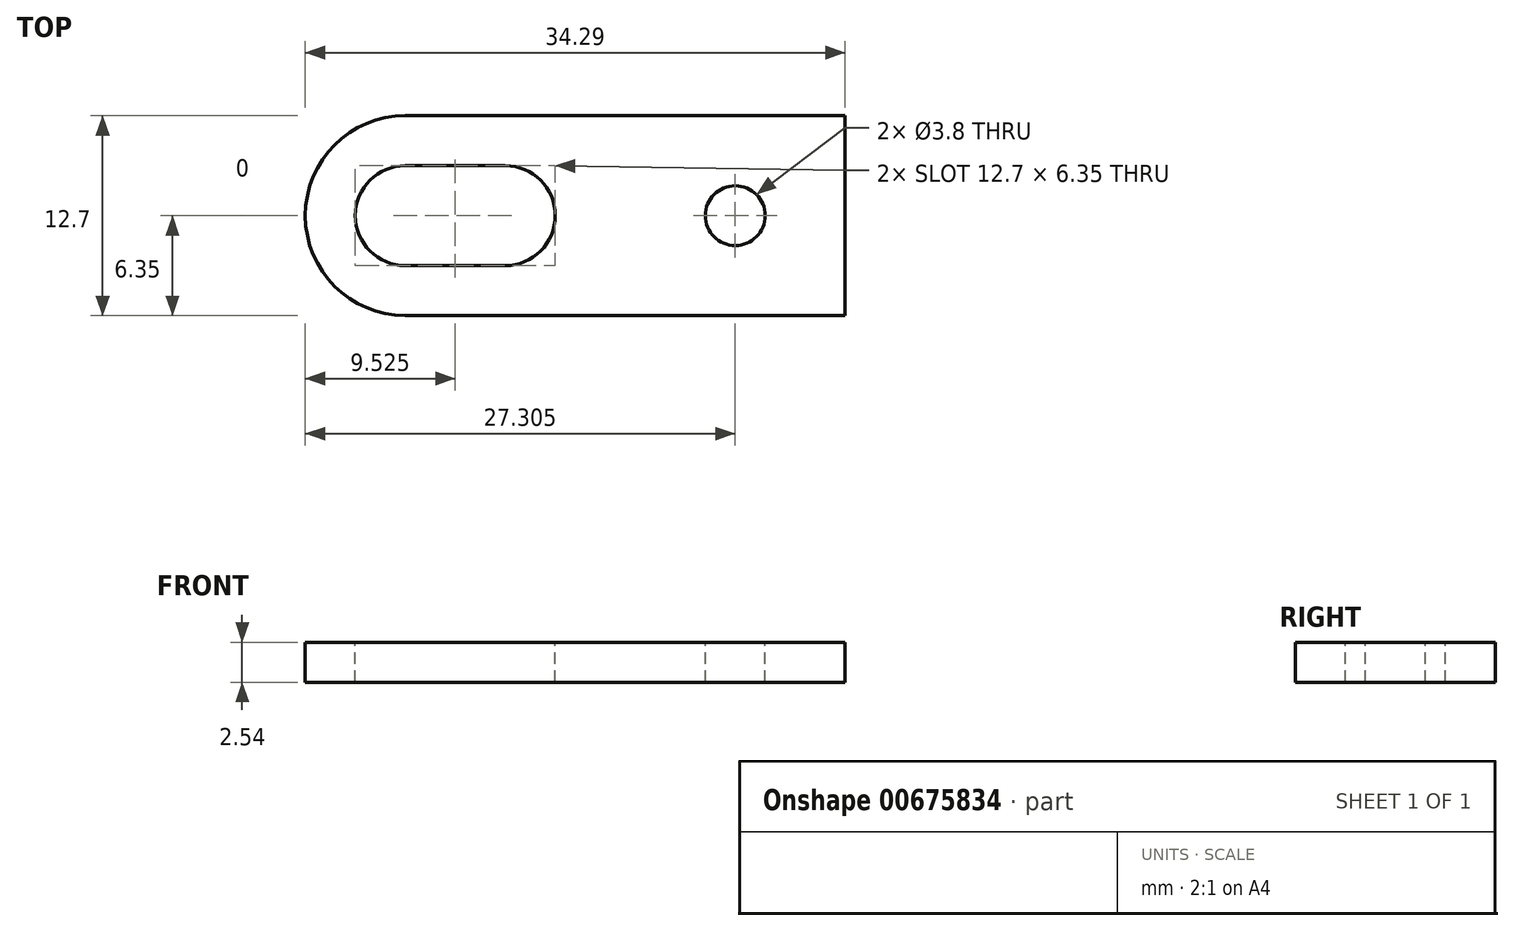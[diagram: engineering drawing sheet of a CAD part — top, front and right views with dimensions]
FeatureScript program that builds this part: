
annotation { "Feature Type Name" : "Feature", "Feature Type Description" : "" }
export const myFeature = defineFeature(function(context is Context, id is Id, definition is map)
    precondition{}
    {
        {
            var Q0;
            Q0=qCreatedBy(makeId("Top.planeOp"),FACE);
            var sketch = newSketch(context, id + "F0", { "sketchPlane" : qUnion([Q0])});
            skLineSegment(sketch, "E0.bottom", {"start": v(6.35, 0) * mm, "end": v(34.3, 0) * mm});
            skLineSegment(sketch, "E0.top", {"start": v(6.35, 12.7) * mm, "end": v(34.3, 12.7) * mm});
            skLineSegment(sketch, "E0.left", {"start": v(0, 6.35) * mm, "end": v(0, 6.35) * mm});
            skLineSegment(sketch, "E0.right", {"start": v(34.3, 0) * mm, "end": v(34.3, 12.7) * mm});
            skPoint(sketch, "E1.visualSharp", {"position": v(0, 12.7) * mm});
            skArc(sketch, "E1.filletArc", {"start": v(6.35, 12.7) * mm, "mid": v(1.86, 10.84) * mm, "end": v(0, 6.35) * mm});
            skPoint(sketch, "E2.visualSharp", {"position": v(0, 0) * mm});
            skArc(sketch, "E2.filletArc", {"start": v(0, 6.35) * mm, "mid": v(1.86, 1.86) * mm, "end": v(6.35, 0) * mm});
            skPoint(sketch, "E3.visualSharp", {"position": v(34.3, 12.7) * mm});
            skSolve(sketch);
        }
        {
            var Q0;
            Q0=qSketchRegion(id+"F0",true);
            extrude(context, id + "F1", {"entities" : qUnion([Q0]), "depth" : 2.54 * mm, "offsetDistance" : 25.4 * mm});
        }
        {
            var Q0;
            Q0=makeQuery(id+"F1.opExtrude","CAP_FACE",FACE,{"disambiguationData":[OSD([sQuery(id+"F0.wireOp",EDGE,"E0.bottom"),sQuery(id+"F0.wireOp",EDGE,"E0.top"),sQuery(id+"F0.wireOp",EDGE,"E0.left"),sQuery(id+"F0.wireOp",EDGE,"E0.right")])],"isStart":false});
            var sketch = newSketch(context, id + "F2", { "sketchPlane" : qUnion([Q0])});
            skArc(sketch, "E4", {"start": v(6.35, 9.53) * mm, "mid": v(3.17, 6.35) * mm, "end": v(6.35, 3.18) * mm});
            skLineSegment(sketch, "E5", {"start": v(0, 6.35) * mm, "end": v(34.3, 6.35) * mm, "construction": true});
            skArc(sketch, "E6", {"start": v(12.7, 3.18) * mm, "mid": v(15.87, 6.35) * mm, "end": v(12.7, 9.53) * mm});
            skLineSegment(sketch, "E7", {"start": v(6.35, 9.53) * mm, "end": v(12.7, 9.53) * mm});
            skLineSegment(sketch, "E8", {"start": v(12.7, 3.18) * mm, "end": v(6.35, 3.18) * mm});
            skSolve(sketch);
        }
        {
            var Q0;
            Q0=qSketchRegion(id+"F2",true);
            extrude(context, id + "F3", {"entities" : qUnion([Q0]), "operationType" : NewBodyOperationType.REMOVE, "endBound" : BoundingType.THROUGH_ALL, "oppositeDirection" : true, "depth" : 25.4 * mm, "offsetDistance" : 25.4 * mm});
        }
        {
            var Q0;
            Q0=makeQuery(id+"F1.opExtrude","CAP_FACE",FACE,{"disambiguationData":[OSD([sQuery(id+"F0.wireOp",EDGE,"E0.bottom"),sQuery(id+"F0.wireOp",EDGE,"E0.top"),sQuery(id+"F0.wireOp",EDGE,"E0.left"),sQuery(id+"F0.wireOp",EDGE,"E0.right")])],"isStart":false});
            var sketch = newSketch(context, id + "F4", { "sketchPlane" : qUnion([Q0])});
            skPoint(sketch, "E9", {"position": v(27.3, 6.35) * mm});
            skLineSegment(sketch, "E10", {"start": v(0, 6.35) * mm, "end": v(34.3, 6.35) * mm, "construction": true});
            skLineSegment(sketch, "E11", {"start": v(9.53, 9.52) * mm, "end": v(9.53, 3.17) * mm, "construction": true});
            skSolve(sketch);
        }
        {
            var Q0;
            Q0=sQuery(id+"F4.wireOp",VERTEX,"E9");
            var Q1;
            Q1=makeQuery(id+"F1.opExtrude","SWEPT_BODY",BODY,{"disambiguationData":[OSD([sQuery(id+"F0.wireOp",EDGE,"E0.bottom"),sQuery(id+"F0.wireOp",EDGE,"E0.top"),sQuery(id+"F0.wireOp",EDGE,"E0.left"),sQuery(id+"F0.wireOp",EDGE,"E0.right")])]});
            hole(context, id + "F5", {"style" : HoleStyle.SIMPLE, "endStyle" : HoleEndStyle.THROUGH, "standardTappedOrClearance" : lookupTablePath({ "standard" : "ANSI", "fit" : "Normal (ASME)", "size" : "#6", "type" : "Clearance" }), "standardBlindInLast" : lookupTablePath({ "fit" : "Free", "standard" : "ANSI", "size" : "#6", "type" : "Clearance" }), "holeDiameter" : 3.8 * mm, "majorDiameter" : 3.5 * mm, "isTappedThrough" : true, "tappedDepth" : 10.32 * mm, "tapClearance" : 3, "startFromSketch" : true, "locations" : qUnion([Q0]), "scope" : qUnion([Q1])});
        }
    });
